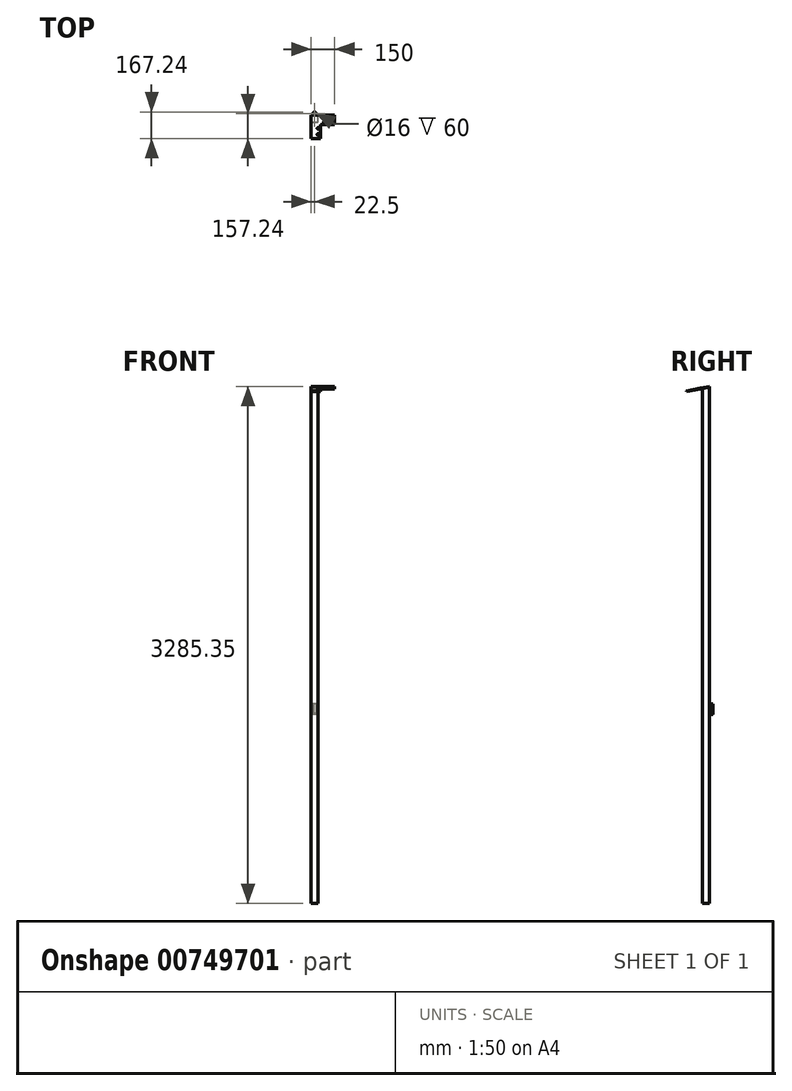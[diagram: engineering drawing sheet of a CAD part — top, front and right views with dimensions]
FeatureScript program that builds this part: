
annotation { "Feature Type Name" : "Feature", "Feature Type Description" : "" }
export const myFeature = defineFeature(function(context is Context, id is Id, definition is map)
    precondition{}
    {
        {
            var Q0;
            Q0=qCreatedBy(makeId("Top.planeOp"),FACE);
            var sketch = newSketch(context, id + "F0", { "sketchPlane" : qUnion([Q0])});
            skLineSegment(sketch, "E0.bottom", {"start": v(22.5, -22.5) * mm, "end": v(-22.5, -22.5) * mm});
            skLineSegment(sketch, "E0.top", {"start": v(22.5, 22.5) * mm, "end": v(-22.5, 22.5) * mm});
            skLineSegment(sketch, "E0.left", {"start": v(22.5, -22.5) * mm, "end": v(22.5, 22.5) * mm});
            skLineSegment(sketch, "E0.right", {"start": v(-22.5, -22.5) * mm, "end": v(-22.5, 22.5) * mm});
            skPoint(sketch, "E0.middle", {"position": v(0, 0) * mm});
            skSolve(sketch);
        }
        {
            var Q0;
            Q0=qSketchRegion(id+"F0",true);
            extrude(context, id + "F1", {"entities" : qUnion([Q0]), "depth" : 3330 * mm, "offsetDistance" : 25 * mm});
        }
        {
            var Q0;
            Q0=makeQuery(id+"F1.opExtrude","CAP_EDGE",EDGE,{"disambiguationData":[OSD([sQuery(id+"F0.wireOp",EDGE,"E0.bottom")])],"isStart":false});
            cPlane(context, id + "F2", {"entities" : qUnion([Q0]), "cplaneType" : CPlaneType.LINE_ANGLE, "offset" : 25 * mm, "angle" : 101 * degree, "oppositeDirection" : true, "width" : 150 * mm, "height" : 150 * mm});
        }
        {
            var Q0;
            Q0=makeQuery(id+"F1.opExtrude","CAP_FACE",FACE,{"disambiguationData":[OSD([sQuery(id+"F0.wireOp",EDGE,"E0.bottom"),sQuery(id+"F0.wireOp",EDGE,"E0.top"),sQuery(id+"F0.wireOp",EDGE,"E0.left"),sQuery(id+"F0.wireOp",EDGE,"E0.right")])],"isStart":false});
            var sketch = newSketch(context, id + "F3", { "sketchPlane" : qUnion([Q0])});
            skLineSegment(sketch, "E1.bottom", {"start": v(-22.5, 22.5) * mm, "end": v(22.5, 22.5) * mm});
            skLineSegment(sketch, "E1.top", {"start": v(-22.5, -22.5) * mm, "end": v(22.5, -22.5) * mm});
            skLineSegment(sketch, "E1.left", {"start": v(-22.5, 22.5) * mm, "end": v(-22.5, -22.5) * mm});
            skLineSegment(sketch, "E1.right", {"start": v(22.5, 22.5) * mm, "end": v(22.5, -22.5) * mm});
            skSolve(sketch);
        }
        {
            var Q0;
            Q0=qCreatedBy(id+"F2.planeOp",FACE);
            var sketch = newSketch(context, id + "F4", { "sketchPlane" : qUnion([Q0])});
            skLineSegment(sketch, "E2.bottom", {"start": v(-22.5, -659.15) * mm, "end": v(22.5, -659.15) * mm});
            skLineSegment(sketch, "E2.top", {"start": v(-22.5, -613.3) * mm, "end": v(22.5, -613.3) * mm});
            skLineSegment(sketch, "E2.left", {"start": v(-22.5, -659.15) * mm, "end": v(-22.5, -613.3) * mm});
            skLineSegment(sketch, "E2.right", {"start": v(22.5, -659.15) * mm, "end": v(22.5, -613.3) * mm});
            skSolve(sketch);
        }
        {
            var Q0;
            Q0=makeQuery(id+"F4.imprint","IMPRINT",FACE,{"disambiguationData":[TD([[makeQuery(id+"F4.imprint","IMPRINT",EDGE,{"derivedFrom":sQuery(id+"F4.wireOp",EDGE,"E2.bottom")}),1.0]])]});
            extrude(context, id + "F5", {"entities" : qUnion([Q0]), "operationType" : NewBodyOperationType.ADD, "depth" : 25 * mm, "offsetDistance" : 25 * mm});
        }
        {
            var Q0;
            Q0=qCreatedBy(id+"F2.planeOp",FACE);
            var sketch = newSketch(context, id + "F6", { "sketchPlane" : qUnion([Q0])});
            skLineSegment(sketch, "E3.bottom", {"start": v(-22.5, -659.15) * mm, "end": v(37.5, -659.15) * mm});
            skLineSegment(sketch, "E3.top", {"start": v(-22.5, -599.15) * mm, "end": v(37.5, -599.15) * mm});
            skLineSegment(sketch, "E3.left", {"start": v(-22.5, -659.15) * mm, "end": v(-22.5, -599.15) * mm});
            skLineSegment(sketch, "E3.right", {"start": v(37.5, -659.15) * mm, "end": v(37.5, -599.15) * mm});
            skLineSegment(sketch, "E4.bottom", {"start": v(37.5, -659.15) * mm, "end": v(127.5, -659.15) * mm});
            skLineSegment(sketch, "E4.top", {"start": v(37.5, -599.15) * mm, "end": v(127.5, -599.15) * mm});
            skLineSegment(sketch, "E4.right", {"start": v(127.5, -659.15) * mm, "end": v(127.5, -599.15) * mm});
            skLineSegment(sketch, "E5.top", {"start": v(-22.5, -509.15) * mm, "end": v(37.5, -509.15) * mm});
            skLineSegment(sketch, "E5.left", {"start": v(-22.5, -599.15) * mm, "end": v(-22.5, -509.15) * mm});
            skLineSegment(sketch, "E5.right", {"start": v(37.5, -599.15) * mm, "end": v(37.5, -509.15) * mm});
            skLineSegment(sketch, "E6", {"start": v(-22.5, -659.15) * mm, "end": v(-22.5, -509.15) * mm});
            skSolve(sketch);
        }
        {
            var Q0;
            Q0=qSketchRegion(id+"F6",true);
            extrude(context, id + "F7", {"entities" : qUnion([Q0]), "operationType" : NewBodyOperationType.ADD, "depth" : 5 * mm, "offsetDistance" : 25 * mm});
        }
        {
            var Q0;
            Q0=makeQuery(id+"F7.boolean.opBoolean","MERGE",FACE,{"derivedFrom":[makeQuery(id+"F5.opExtrude","CAP_FACE",FACE,{"disambiguationData":[OSD([sQuery(id+"F4.wireOp",EDGE,"E2.bottom"),sQuery(id+"F4.wireOp",EDGE,"E2.top"),sQuery(id+"F4.wireOp",EDGE,"E2.left"),sQuery(id+"F4.wireOp",EDGE,"E2.right")])],"isStart":true}),makeQuery(id+"F7.opExtrude","CAP_FACE",FACE,{"disambiguationData":[OSD([sQuery(id+"F6.wireOp",EDGE,"E3.bottom"),sQuery(id+"F6.wireOp",EDGE,"E4.bottom"),sQuery(id+"F6.wireOp",EDGE,"E4.top"),sQuery(id+"F6.wireOp",EDGE,"E4.right"),sQuery(id+"F6.wireOp",EDGE,"E5.top"),sQuery(id+"F6.wireOp",EDGE,"E5.right"),sQuery(id+"F6.wireOp",EDGE,"E6")])],"isStart":true})]});
            var sketch = newSketch(context, id + "F8", { "sketchPlane" : qUnion([Q0])});
            skLineSegment(sketch, "E7", {"start": v(37.5, 509.15) * mm, "end": v(37.5, 534.15) * mm});
            skLineSegment(sketch, "E8", {"start": v(37.5, 534.15) * mm, "end": v(22.5, 534.15) * mm});
            skLineSegment(sketch, "E9", {"start": v(22.5, 534.15) * mm, "end": v(22.5, 574.15) * mm});
            skCircle(sketch, "E10", {"center": v(22.5, 534.15) * mm, "radius": 6 * mm});
            skCircle(sketch, "E11", {"center": v(22.5, 574.15) * mm, "radius": 6 * mm});
            skLineSegment(sketch, "E12", {"start": v(127.5, 599.15) * mm, "end": v(102.5, 599.15) * mm});
            skLineSegment(sketch, "E13", {"start": v(102.5, 599.15) * mm, "end": v(102.5, 614.15) * mm});
            skLineSegment(sketch, "E14", {"start": v(102.5, 614.15) * mm, "end": v(62.5, 614.15) * mm});
            skCircle(sketch, "E15", {"center": v(102.5, 614.15) * mm, "radius": 6 * mm});
            skCircle(sketch, "E16", {"center": v(62.5, 614.15) * mm, "radius": 6 * mm});
            skSolve(sketch);
        }
        {
            var Q0;
            Q0=qSketchRegion(id+"F8",true);
            extrude(context, id + "F9", {"entities" : qUnion([Q0]), "operationType" : NewBodyOperationType.REMOVE, "oppositeDirection" : true, "depth" : 25 * mm, "offsetDistance" : 25 * mm});
        }
        {
            var Q0;
            Q0=qCreatedBy(makeId("Top.planeOp"),FACE);
            var sketch = newSketch(context, id + "F10", { "sketchPlane" : qUnion([Q0])});
            skLineSegment(sketch, "E17.bottom", {"start": v(-22.5, 22.5) * mm, "end": v(127.5, 22.5) * mm});
            skLineSegment(sketch, "E17.top", {"start": v(-22.5, 27.27) * mm, "end": v(127.5, 27.27) * mm});
            skLineSegment(sketch, "E17.left", {"start": v(-22.5, 22.5) * mm, "end": v(-22.5, 27.27) * mm});
            skLineSegment(sketch, "E17.right", {"start": v(127.5, 22.5) * mm, "end": v(127.5, 27.27) * mm});
            skSolve(sketch);
        }
        {
            var Q0;
            Q0=qSketchRegion(id+"F10",true);
            extrude(context, id + "F11", {"entities" : qUnion([Q0]), "operationType" : NewBodyOperationType.REMOVE, "depth" : 3358.7 * mm, "offsetDistance" : 25 * mm});
        }
        {
            var Q0;
            Q0=makeQuery(id+"F1.opExtrude","CAP_FACE",FACE,{"disambiguationData":[OSD([sQuery(id+"F0.wireOp",EDGE,"E0.bottom"),sQuery(id+"F0.wireOp",EDGE,"E0.top"),sQuery(id+"F0.wireOp",EDGE,"E0.left"),sQuery(id+"F0.wireOp",EDGE,"E0.right")])],"isStart":true});
            var sketch = newSketch(context, id + "F12", { "sketchPlane" : qUnion([Q0])});
            skLineSegment(sketch, "E18.bottom", {"start": v(22.5, 22.5) * mm, "end": v(-22.5, 22.5) * mm});
            skLineSegment(sketch, "E18.top", {"start": v(22.5, -22.5) * mm, "end": v(-22.5, -22.5) * mm});
            skLineSegment(sketch, "E18.left", {"start": v(22.5, 22.5) * mm, "end": v(22.5, -22.5) * mm});
            skLineSegment(sketch, "E18.right", {"start": v(-22.5, 22.5) * mm, "end": v(-22.5, -22.5) * mm});
            skSolve(sketch);
        }
        {
            var Q0;
            Q0 = qSketchRegion(id + "F12", true);
            extrude(context, id + "F13", {"entities" : qUnion([Q0]), "operationType" : NewBodyOperationType.REMOVE, "oppositeDirection" : true, "depth" : ((333 - 281.5) + 1.9) * mm, "offsetDistance" : 25 * mm});
        }
        {
            var Q0;
            Q0=qCreatedBy(makeId("Top.planeOp"),FACE);
            cPlane(context, id + "F14", {"entities" : qUnion([Q0]), "cplaneType" : CPlaneType.OFFSET, "offset" : 1256 * mm, "width" : 150 * mm, "height" : 150 * mm});
        }
        {
            var Q0;
            Q0=qCreatedBy(id+"F14.planeOp",FACE);
            var sketch = newSketch(context, id + "F15", { "sketchPlane" : qUnion([Q0])});
            skLineSegment(sketch, "E19", {"start": v(22.5, 22.5) * mm, "end": v(-22.5, 22.5) * mm});
            skLineSegment(sketch, "E20", {"start": v(0, 22.5) * mm, "end": v(0, 32.5) * mm});
            skLineSegment(sketch, "E21", {"start": v(0, 22.5) * mm, "end": v(-10, 22.5) * mm});
            skLineSegment(sketch, "E22", {"start": v(0, 22.5) * mm, "end": v(10, 22.5) * mm});
            skCircle(sketch, "E23", {"center": v(0, 32.5) * mm, "radius": 10 * mm});
            skLineSegment(sketch, "E24", {"start": v(10, 22.5) * mm, "end": v(10, 32.5) * mm});
            skLineSegment(sketch, "E25", {"start": v(-10, 22.5) * mm, "end": v(-10, 32.5) * mm});
            skSolve(sketch);
        }
        {
            var Q0;
            Q0 = qSketchRegion(id + "F15", true);
            extrude(context, id + "F16", {"entities" : qUnion([Q0]), "operationType" : NewBodyOperationType.ADD, "depth" : 5 * mm, "offsetDistance" : 25 * mm});
        }
        {
            var Q0;
            Q0=makeQuery(id+"F16.opExtrude","CAP_FACE",FACE,{"disambiguationData":[OSD([sQuery(id+"F15.wireOp",EDGE,"E21"),sQuery(id+"F15.wireOp",EDGE,"E22"),sQuery(id+"F15.wireOp",EDGE,"E23"),sQuery(id+"F15.wireOp",EDGE,"E24"),sQuery(id+"F15.wireOp",EDGE,"E25")])],"isStart":false});
            var sketch = newSketch(context, id + "F17", { "sketchPlane" : qUnion([Q0])});
            skArc(sketch, "E26.0", {"start": v(10, 32.5) * mm, "mid": v(0, 42.5) * mm, "end": v(-10, 32.5) * mm});
            skLineSegment(sketch, "E27", {"start": v(10, 32.5) * mm, "end": v(-10, 32.5) * mm});
            skArc(sketch, "E28.MirrorCS", {"start": v(10, 32.5) * mm, "mid": v(0, 22.5) * mm, "end": v(-10, 32.5) * mm});
            skLineSegment(sketch, "E29", {"start": v(-10, 22.5) * mm, "end": v(10, 22.5) * mm});
            skLineSegment(sketch, "E30", {"start": v(10, 22.5) * mm, "end": v(10, 32.5) * mm});
            skLineSegment(sketch, "E31", {"start": v(-10, 22.5) * mm, "end": v(-10, 32.5) * mm});
            skArc(sketch, "E32.0", {"start": v(8, 32.5) * mm, "mid": v(0, 40.5) * mm, "end": v(-8, 32.5) * mm});
            skArc(sketch, "E33.MirrorCS", {"start": v(8, 32.5) * mm, "mid": v(0, 24.5) * mm, "end": v(-8, 32.5) * mm});
            skSolve(sketch);
        }
        {
            var Q0;
            Q0 = qSketchRegion(id + "F17", true);
            extrude(context, id + "F18", {"entities" : qUnion([Q0]), "operationType" : NewBodyOperationType.ADD, "depth" : 60 * mm, "offsetDistance" : 25 * mm});
        }
    });
